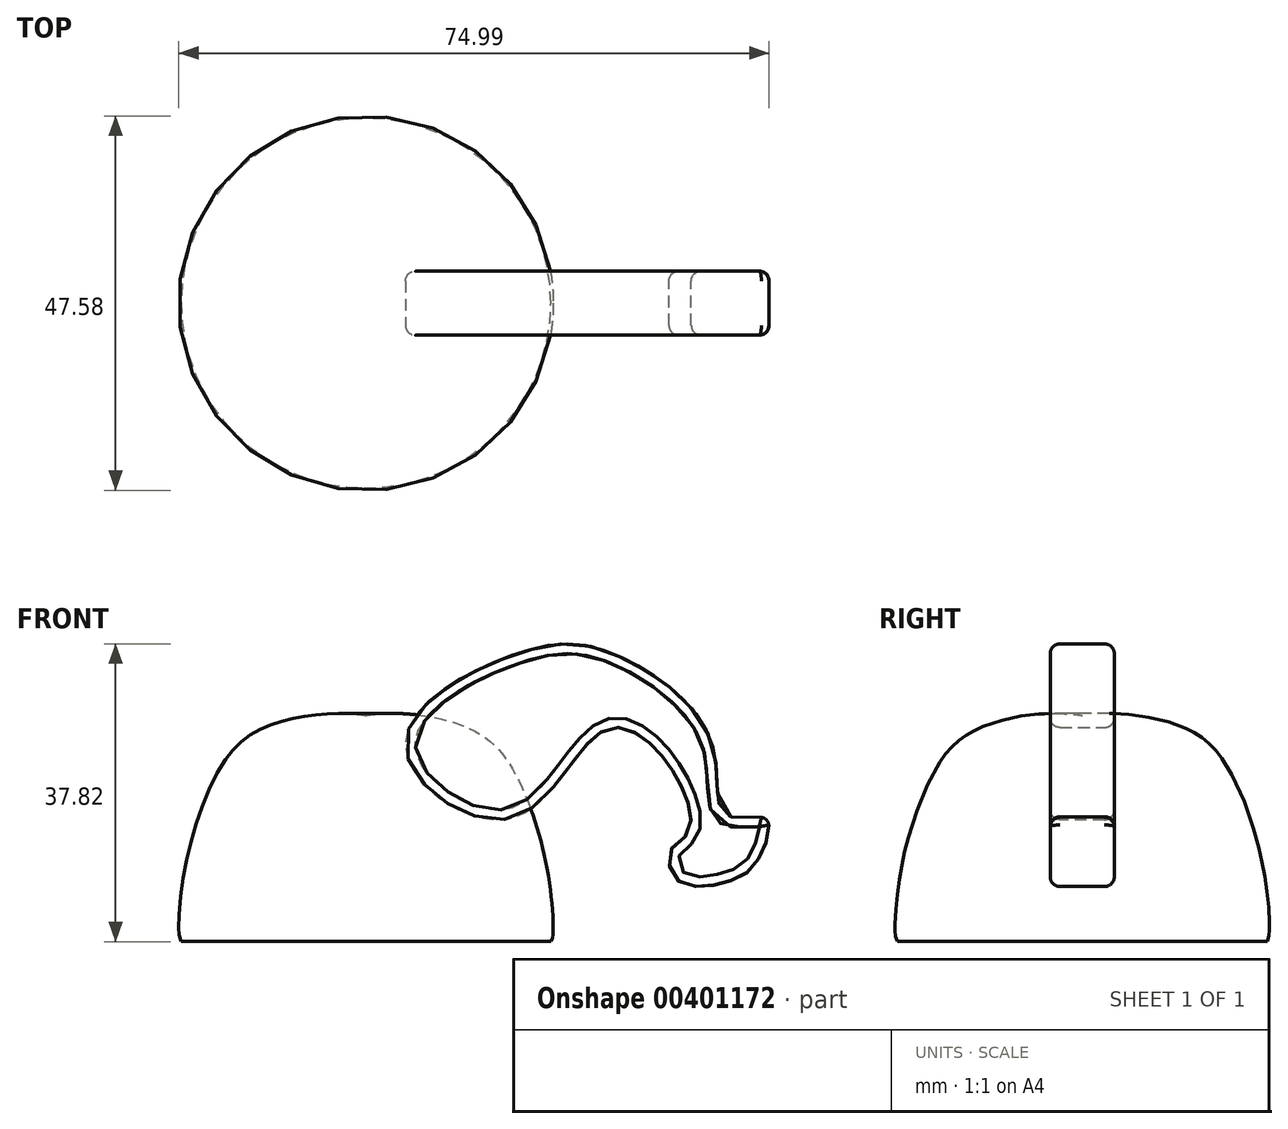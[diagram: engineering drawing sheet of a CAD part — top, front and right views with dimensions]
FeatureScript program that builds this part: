
annotation { "Feature Type Name" : "Feature", "Feature Type Description" : "" }
export const myFeature = defineFeature(function(context is Context, id is Id, definition is map)
    precondition{}
    {
        {
            var Q0;
            Q0=qCreatedBy(makeId("Front.planeOp"),FACE);
            var sketch = newSketch(context, id + "F0", { "sketchPlane" : qUnion([Q0])});
            skLineSegment(sketch, "E0", {"start": v(0, 73.7) * mm, "end": v(0, -69.17) * mm});
            skFitSpline(sketch, "E1", {"points": [v(0, 35.98) * mm, v(13.2, 34.3) * mm, v(18.72, 28.97) * mm, v(23.12, 15.86) * mm, v(23.49, 7.23) * mm, v(23.15, 7.2) * mm], "startDerivative": vector(51.87, 7.46) * mm, "endDerivative": vector(-6.9, 2.71) * mm});
            skLineSegment(sketch, "E2", {"start": v(23.49, 7.23) * mm, "end": v(0, 7.23) * mm});
            skLineSegment(sketch, "E3", {"start": v(0, 4.14) * mm, "end": v(25.03, 4.14) * mm});
            skLineSegment(sketch, "E4", {"start": v(25.03, 4.14) * mm, "end": v(23.49, 7.23) * mm});
            skLineSegment(sketch, "E5", {"start": v(0, 7.23) * mm, "end": v(0, 4.14) * mm});
            skSolve(sketch);
        }
        {
            var Q0;
            {var subQ3=sQuery(id+"F0.wireOp",EDGE,"E2");Q0=makeQuery(id+"F0.imprint","IMPRINT",FACE,{"disambiguationData":[TD([[makeQuery(id+"F0.imprint","IMPRINT",EDGE,{"derivedFrom":subQ3}),-1.0]])]});}
            var Q1;
            Q1=sQuery(id+"F0.wireOp",EDGE,"E0");
            revolve(context, id + "F1", {"entities" : qUnion([Q0]), "axis" : qUnion([Q1]), "revolveType" : RevolveType.FULL});
        }
        {
            var Q0;
            Q0=qCreatedBy(makeId("Front.planeOp"),FACE);
            var sketch = newSketch(context, id + "F2", { "sketchPlane" : qUnion([Q0])});
            skFitSpline(sketch, "E6", {"points": [v(5.04, 32.11) * mm, v(19.36, 43.86) * mm, v(31.4, 43.8) * mm, v(43.92, 32.44) * mm, v(45.66, 23.3) * mm, v(50.78, 22.8) * mm, v(50.06, 18.06) * mm, v(46.83, 15.16) * mm, v(39.72, 14.92) * mm, v(38.84, 19.1) * mm, v(41.07, 21.23) * mm, v(38.52, 29.6) * mm, v(30.35, 34.12) * mm, v(18.42, 22.91) * mm, v(5.04, 32.11) * mm]});
            skSolve(sketch);
        }
        {
            var Q0;
            Q0=makeQuery(id+"F2.imprint","IMPRINT",FACE,{"disambiguationData":[TD([[makeQuery(id+"F2.imprint","IMPRINT",EDGE,{"derivedFrom":sQuery(id+"F2.wireOp",EDGE,"E6")}),-1.0]])]});
            extrude(context, id + "F3", {"entities" : qUnion([Q0]), "endBound" : BoundingType.SYMMETRIC, "depth" : 8.13 * mm});
        }
        {
            var Q0;
            Q0=makeQuery(id+"F3.opExtrude","CAP_EDGE",EDGE,{"disambiguationData":[OSD([sQuery(id+"F2.wireOp",EDGE,"E6")])],"isStart":false});
            var Q1;
            Q1=makeQuery(id+"F3.opExtrude","CAP_EDGE",EDGE,{"disambiguationData":[OSD([sQuery(id+"F2.wireOp",EDGE,"E6")])],"isStart":true});
            fillet(context, id + "F4", {"entities" : qUnion([Q0, Q1]), "radius" : 1.23 * mm, "tangentPropagation" : true, "allowEdgeOverflow" : false});
        }
    });
